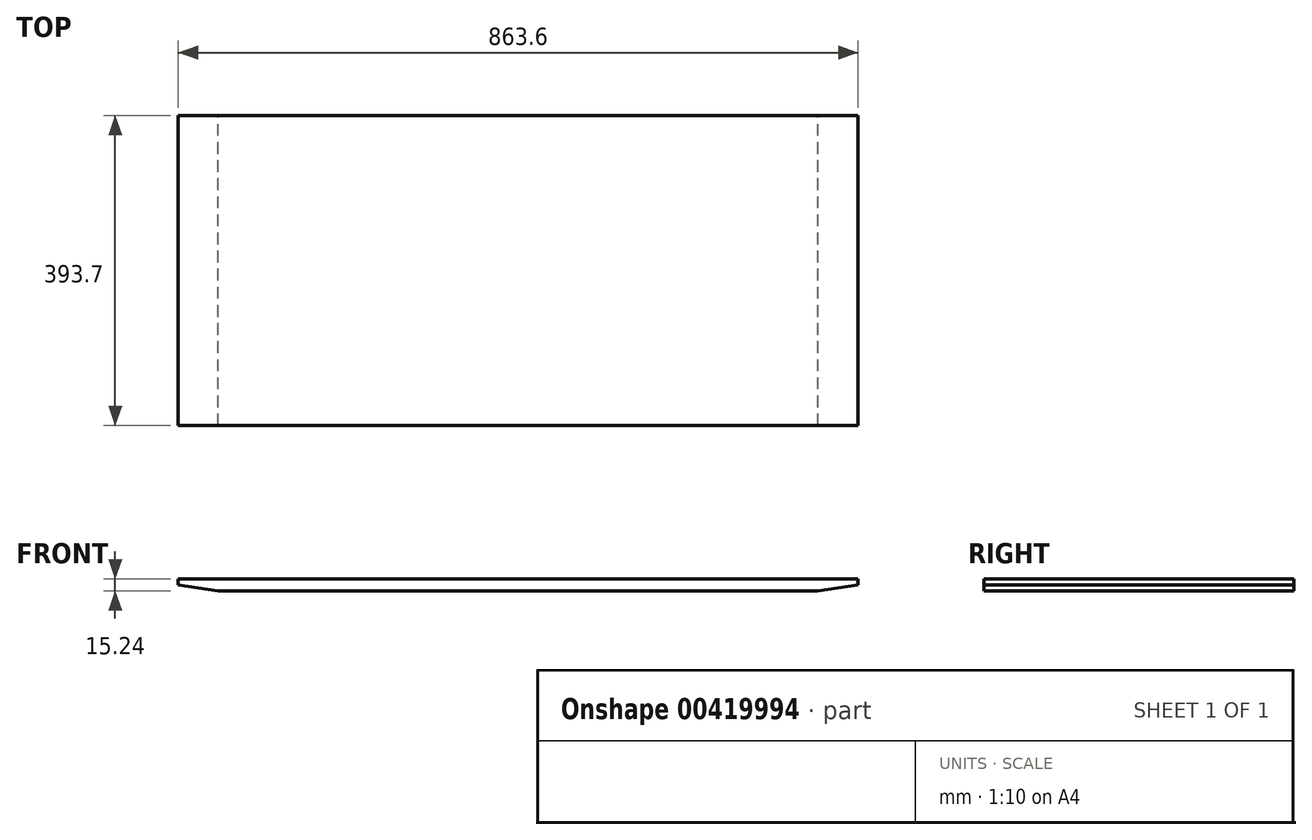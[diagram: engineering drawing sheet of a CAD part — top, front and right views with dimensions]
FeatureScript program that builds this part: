
annotation { "Feature Type Name" : "Feature", "Feature Type Description" : "" }
export const myFeature = defineFeature(function(context is Context, id is Id, definition is map)
    precondition{}
    {
        {
            var Q0;
            Q0=qCreatedBy(makeId("Top.planeOp"),FACE);
            var sketch = newSketch(context, id + "F0", { "sketchPlane" : qUnion([Q0])});
            skLineSegment(sketch, "E0.bottom", {"start": v(431.8, -196.85) * mm, "end": v(-431.8, -196.85) * mm});
            skLineSegment(sketch, "E0.top", {"start": v(431.8, 196.85) * mm, "end": v(-431.8, 196.85) * mm});
            skLineSegment(sketch, "E0.left", {"start": v(431.8, -196.85) * mm, "end": v(431.8, 196.85) * mm});
            skLineSegment(sketch, "E0.right", {"start": v(-431.8, -196.85) * mm, "end": v(-431.8, 196.85) * mm});
            skPoint(sketch, "E0.middle", {"position": v(0, 0) * mm});
            skSolve(sketch);
        }
        {
            var Q0;
            Q0=makeQuery(id+"F0.imprint","IMPRINT",FACE,{"disambiguationData":[TD([[makeQuery(id+"F0.imprint","IMPRINT",EDGE,{"derivedFrom":sQuery(id+"F0.wireOp",EDGE,"E0.bottom")}),-1.0]])]});
            extrude(context, id + "F1", {"entities" : qUnion([Q0]), "depth" : 15.24 * mm});
        }
        {
            var Q0;
            Q0=makeQuery(id+"F1.opExtrude","SWEPT_FACE",FACE,{"disambiguationData":[OSD([sQuery(id+"F0.wireOp",EDGE,"E0.top")])]});
            var sketch = newSketch(context, id + "F2", { "sketchPlane" : qUnion([Q0])});
            skLineSegment(sketch, "E1", {"start": v(-431.8, 7.62) * mm, "end": v(-381, 0) * mm});
            skLineSegment(sketch, "E2", {"start": v(-381, 0) * mm, "end": v(-431.8, 0) * mm});
            skLineSegment(sketch, "E3", {"start": v(-431.8, 0) * mm, "end": v(-431.8, 7.62) * mm});
            skLineSegment(sketch, "E4", {"start": v(431.8, 7.62) * mm, "end": v(381, 0) * mm});
            skLineSegment(sketch, "E5", {"start": v(381, 0) * mm, "end": v(431.8, 0) * mm});
            skLineSegment(sketch, "E6", {"start": v(431.8, 0) * mm, "end": v(431.8, 7.62) * mm});
            skSolve(sketch);
        }
        {
            var Q0;
            Q0=makeQuery(id+"F2.imprint","IMPRINT",FACE,{"disambiguationData":[TD([[makeQuery(id+"F2.imprint","IMPRINT",EDGE,{"derivedFrom":sQuery(id+"F2.wireOp",EDGE,"E1")}),-1.0]])]});
            var Q1;
            Q1=makeQuery(id+"F2.imprint","IMPRINT",FACE,{"disambiguationData":[TD([[makeQuery(id+"F2.imprint","IMPRINT",EDGE,{"derivedFrom":sQuery(id+"F2.wireOp",EDGE,"E4")}),1.0]])]});
            extrude(context, id + "F3", {"entities" : qUnion([Q0, Q1]), "operationType" : NewBodyOperationType.REMOVE, "endBound" : BoundingType.THROUGH_ALL, "oppositeDirection" : true, "depth" : 25.4 * mm});
        }
    });
